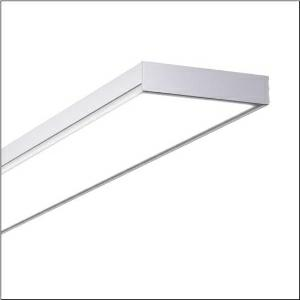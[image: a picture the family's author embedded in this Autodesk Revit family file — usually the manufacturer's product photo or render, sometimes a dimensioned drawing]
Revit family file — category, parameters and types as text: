
# Revit family: apollon_r__31_surface_51mp26wm2441ea_9a05
name_source: partatom
category: Lighting Fixtures
units: mm (PartAtom-declared; Revit-internal decimal feet)

## family parameters
Cut with Voids When Loaded = No
Host = Face
Light Source = No
Part Type = Normal
Room Calculation Point = No
Round Connector Dimension = Use Diameter
Shared = No

## types (1)
- Apollon® 31 Surface (1 x LED, 4600 lm, 33 W, 4000K)
    Apparent Load = 33 VA
    CIE Flux Codes = 61 87 97 97 100
    Color Rendering = 80
    Color Temperature = 4000K
    Default Elevation = 1800 mm
    Description = Apollon® 31 Surface, office luminaire, primary optical cover: micro prismatic cover, of PMMA, light emission: direct distribution, primary light characteristic: symmetric, installation type: surface-mounted, LED, rated luminous flux: 4.600lm, luminous efficacy: 139lm/W, light colour: 840, colour temperature: 4000K, control gear: ON/OFF Multilumen, with terminal, 3-pole, mains connection: 220..240V, AC, 50/60Hz, rated input power: 33W, housing, of sheet steel, coil coated, metallic grey (RAL 9006), length: 1.545mm, width: 200mm, height: 44mm, protection rating (complete): IP20, insulation class (complete): insulation class II (safety insulation), certification: CE, impact resistance: IK02, permissible operating ambient temperature: -20..+40°C, packaging unit: 1 piece
    Height = 44 mm
    Lamp = 1 x LED
    Lamp Light Flux = 4600 lm
    Lamp Power = 33 W
    Lamp count = 1
    Length = 1545 mm
    Luminous efficacy = 139 lm/W
    Manufacturer = Siteco
    ModVariant = No
    Model = 51MP26WM2441EA
    Mounting Place = Ceiling
    Mounting Type = Surface mounted
    Number of Poles = 1
    OnlyDefault = Yes
    Power Factor = 1
    Product Name = Apollon® 31 Surface
    Product group = office luminaire | ceiling mounted
    ProductGroupID = 302
    Protection Class = Protection class II
    Protection Degree = IP 20
    RLX_Detail_Level = 1
    RLX_Emergency_Light_Flux = 0 lm
    RLX_Emergency_Type = 0
    RLX_Emergency_Type_DB = No
    RlxData = <blob elided: 24093 chars, md5=07a05bfb>
    Socket = socket
    Standby Power = 0 W
    System Light Flux = 4600 lm
    System Power = 33 W
    Type Comments = Product without accessories
    Type Image = l_1313654.jpg
    URL = http://relux.com
    VarID = ---
    Voltage = 0 V
    Weight = 0.00 kg
    Width = 200 mm  [stored 0.656168 ft]

note: [stored X ft] marks values corroborated as IEEE doubles in the binary element streams (Revit-internal decimal feet)

## geometry (parser evidence)
native form markers: Blend x4, Sweep x13
no freeform markers — native parametric forms only
